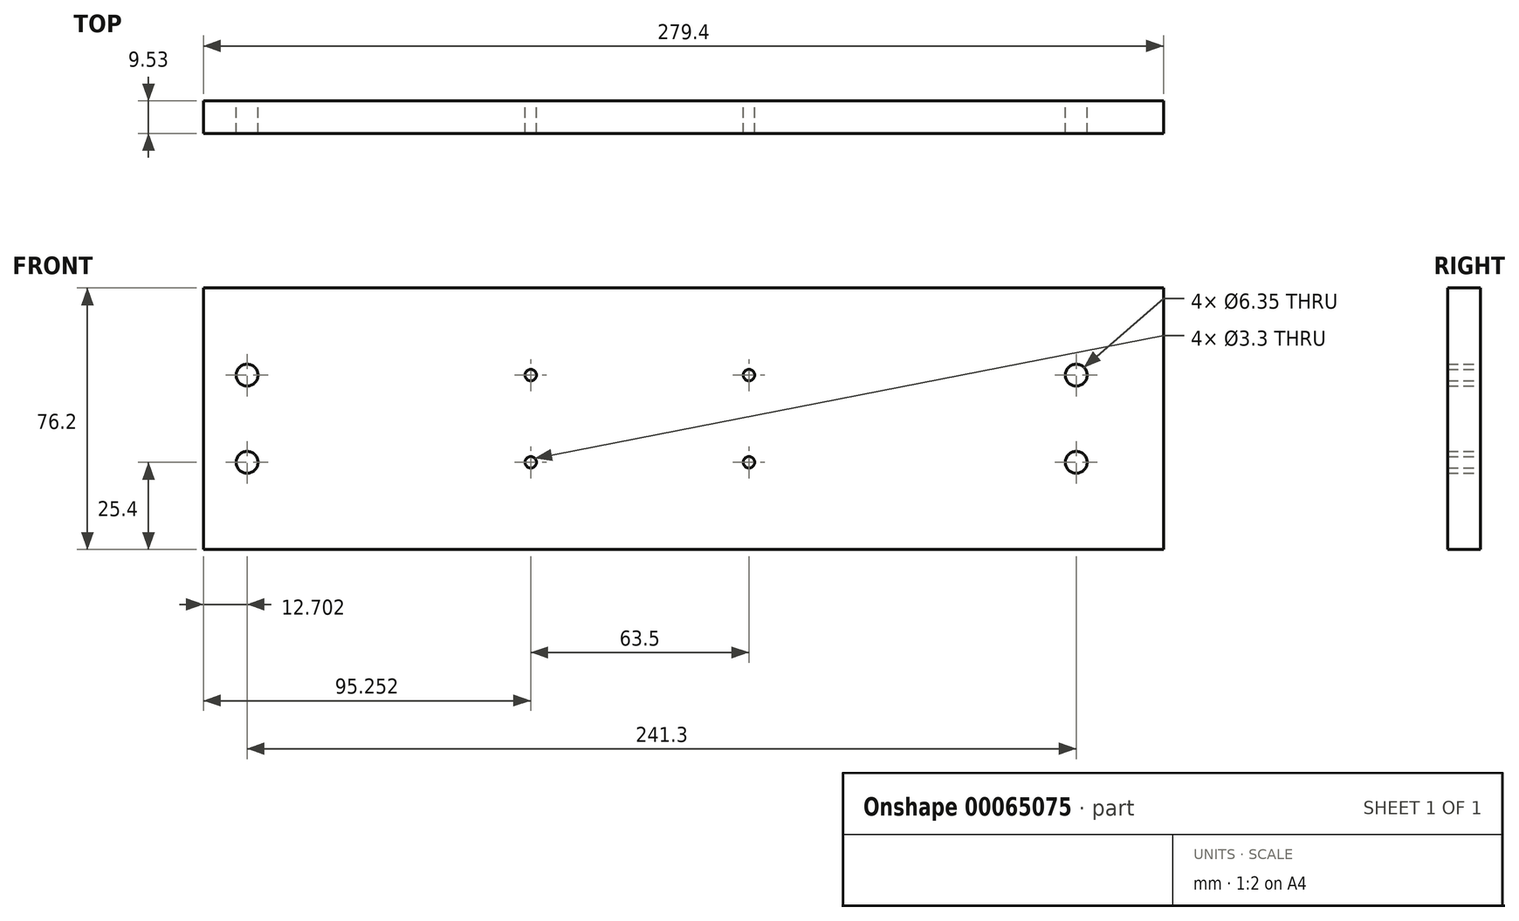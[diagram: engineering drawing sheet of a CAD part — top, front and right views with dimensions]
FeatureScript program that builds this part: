
annotation { "Feature Type Name" : "Feature", "Feature Type Description" : "" }
export const myFeature = defineFeature(function(context is Context, id is Id, definition is map)
    precondition{}
    {
        {
            var Q0;
            Q0=qCreatedBy(makeId("Front.planeOp"),FACE);
            var sketch = newSketch(context, id + "F0", { "sketchPlane" : qUnion([Q0])});
            skLineSegment(sketch, "E0", {"start": v(-154.66, 0) * mm, "end": v(173.47, 0) * mm, "construction": true});
            skLineSegment(sketch, "E1.bottom", {"start": v(-126.39, 38.1) * mm, "end": v(153.01, 38.1) * mm});
            skLineSegment(sketch, "E1.top", {"start": v(-126.39, -38.1) * mm, "end": v(153.01, -38.1) * mm});
            skLineSegment(sketch, "E1.left", {"start": v(-126.39, 38.1) * mm, "end": v(-126.39, -38.1) * mm});
            skLineSegment(sketch, "E1.right", {"start": v(153.01, 38.1) * mm, "end": v(153.01, -38.1) * mm});
            skLineSegment(sketch, "E2", {"start": v(-113.69, 78.15) * mm, "end": v(-113.69, -67.56) * mm, "construction": true});
            skLineSegment(sketch, "E3", {"start": v(-31.14, 81.74) * mm, "end": v(-31.14, -69.36) * mm, "construction": true});
            skLineSegment(sketch, "E4", {"start": v(32.36, 76.65) * mm, "end": v(32.36, -65.17) * mm, "construction": true});
            skLineSegment(sketch, "E5", {"start": v(127.61, 76.35) * mm, "end": v(127.61, -75.34) * mm, "construction": true});
            skLineSegment(sketch, "E6", {"start": v(-145.32, -12.7) * mm, "end": v(196.95, -12.7) * mm, "construction": true});
            skLineSegment(sketch, "E7", {"start": v(-145.32, 12.7) * mm, "end": v(185.29, 12.7) * mm, "construction": true});
            skCircle(sketch, "E8", {"center": v(127.61, 12.7) * mm, "radius": 3.18 * mm});
            skCircle(sketch, "E9", {"center": v(127.61, -12.7) * mm, "radius": 3.18 * mm});
            skCircle(sketch, "E10", {"center": v(32.36, 12.7) * mm, "radius": 1.65 * mm});
            skCircle(sketch, "E11", {"center": v(-31.14, 12.7) * mm, "radius": 1.65 * mm});
            skCircle(sketch, "E12", {"center": v(-31.14, -12.7) * mm, "radius": 1.65 * mm});
            skCircle(sketch, "E13", {"center": v(-113.69, 12.7) * mm, "radius": 3.18 * mm});
            skCircle(sketch, "E14", {"center": v(-113.69, -12.7) * mm, "radius": 3.18 * mm});
            skCircle(sketch, "E15", {"center": v(32.36, -12.7) * mm, "radius": 1.65 * mm});
            skSolve(sketch);
        }
        {
            var Q0;
            Q0=makeQuery(id+"F0.imprint","IMPRINT",FACE,{"disambiguationData":[TD([[makeQuery(id+"F0.imprint","IMPRINT",EDGE,{"derivedFrom":sQuery(id+"F0.wireOp",EDGE,"E1.bottom")}),-1.0]])]});
            extrude(context, id + "F1", {"entities" : qUnion([Q0]), "depth" : 9.52 * mm});
        }
    });
